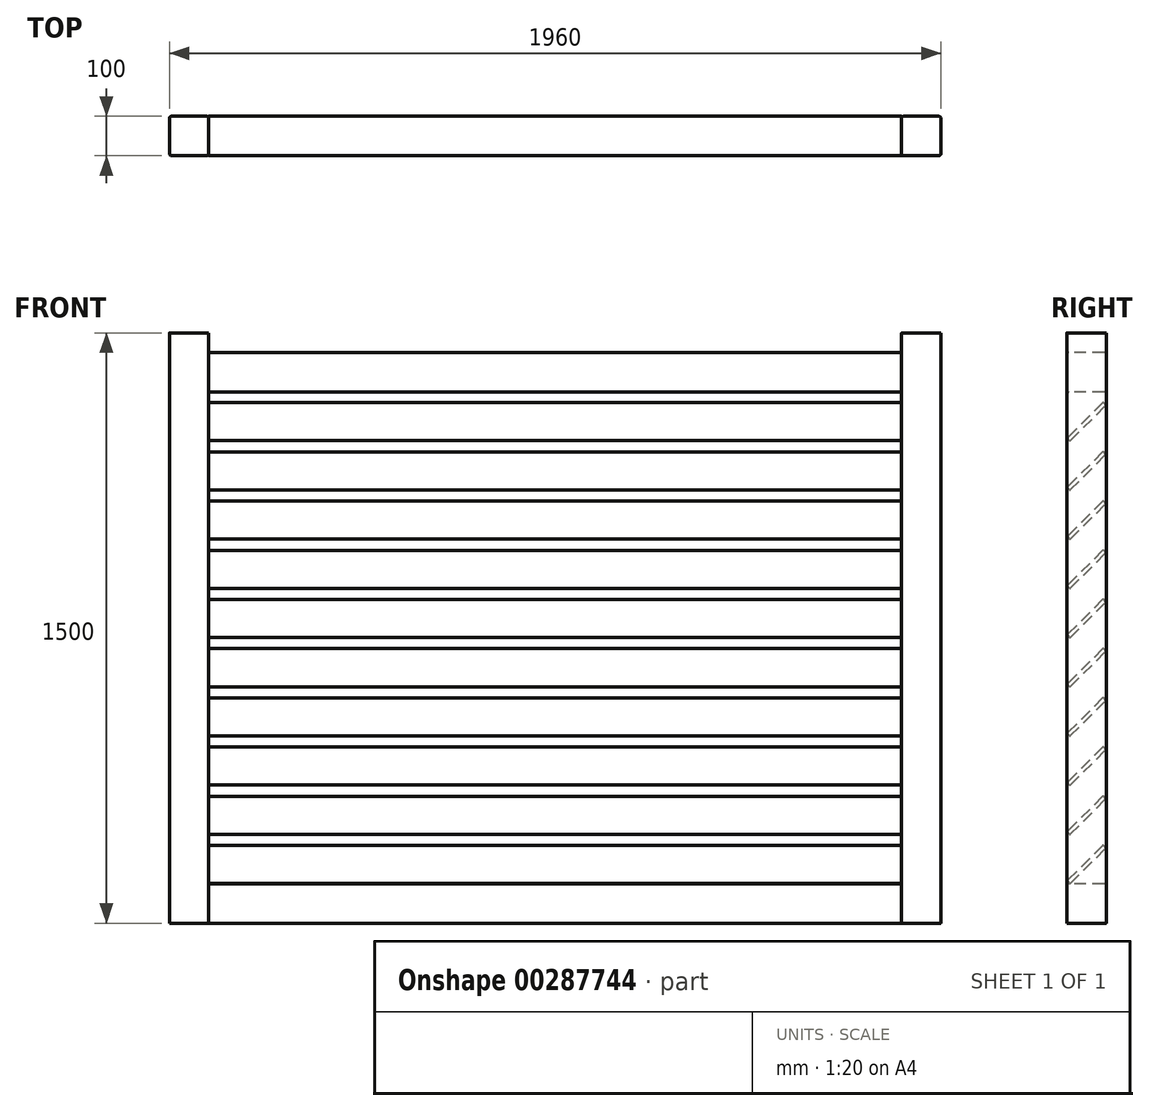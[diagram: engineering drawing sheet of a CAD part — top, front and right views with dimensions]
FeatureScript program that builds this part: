
annotation { "Feature Type Name" : "Feature", "Feature Type Description" : "" }
export const myFeature = defineFeature(function(context is Context, id is Id, definition is map)
    precondition{}
    {
        {
            var Q0;
            Q0=qCreatedBy(makeId("Right.planeOp"),FACE);
            var sketch = newSketch(context, id + "F0", { "sketchPlane" : qUnion([Q0])});
            skLineSegment(sketch, "E0", {"start": v(1.41, 1.41) * mm, "end": v(89.8, 89.8) * mm});
            skLineSegment(sketch, "E1", {"start": v(89.8, 92.63) * mm, "end": v(85.56, 96.87) * mm});
            skLineSegment(sketch, "E2", {"start": v(82.73, 96.87) * mm, "end": v(-5.66, 8.49) * mm});
            skLineSegment(sketch, "E3", {"start": v(-5.66, 5.66) * mm, "end": v(-1.41, 1.41) * mm});
            skPoint(sketch, "E4.visualSharp", {"position": v(84.15, 98.29) * mm});
            skArc(sketch, "E4.filletArc", {"start": v(85.56, 96.87) * mm, "mid": v(84.15, 97.46) * mm, "end": v(82.73, 96.87) * mm});
            skPoint(sketch, "E5.visualSharp", {"position": v(91.22, 91.22) * mm});
            skArc(sketch, "E5.filletArc", {"start": v(89.8, 89.8) * mm, "mid": v(90.39, 91.22) * mm, "end": v(89.8, 92.63) * mm});
            skPoint(sketch, "E6.visualSharp", {"position": v(0, 0) * mm});
            skArc(sketch, "E6.filletArc", {"start": v(-1.41, 1.41) * mm, "mid": v(0, 0.83) * mm, "end": v(1.41, 1.41) * mm});
            skPoint(sketch, "E7.visualSharp", {"position": v(-7.07, 7.07) * mm});
            skArc(sketch, "E7.filletArc", {"start": v(-5.66, 8.49) * mm, "mid": v(-6.24, 7.07) * mm, "end": v(-5.66, 5.66) * mm});
            skLineSegment(sketch, "E8.0.1.0", {"start": v(1.41, 126.41) * mm, "end": v(89.8, 214.8) * mm});
            skLineSegment(sketch, "E8.0.1.1", {"start": v(82.73, 221.87) * mm, "end": v(-5.66, 133.49) * mm});
            skPoint(sketch, "E8.0.1.2", {"position": v(84.15, 223.29) * mm});
            skPoint(sketch, "E8.0.1.3", {"position": v(91.22, 216.22) * mm});
            skPoint(sketch, "E8.0.1.4", {"position": v(-7.07, 132.07) * mm});
            skPoint(sketch, "E8.0.1.5", {"position": v(0, 125) * mm});
            skArc(sketch, "E8.0.1.6", {"start": v(89.8, 214.8) * mm, "mid": v(90.39, 216.22) * mm, "end": v(89.8, 217.63) * mm});
            skArc(sketch, "E8.0.1.7", {"start": v(-1.41, 126.41) * mm, "mid": v(0, 125.83) * mm, "end": v(1.41, 126.41) * mm});
            skArc(sketch, "E8.0.1.8", {"start": v(85.56, 221.87) * mm, "mid": v(84.15, 222.46) * mm, "end": v(82.73, 221.87) * mm});
            skLineSegment(sketch, "E8.0.1.9", {"start": v(-5.66, 130.66) * mm, "end": v(-1.41, 126.41) * mm});
            skArc(sketch, "E8.0.1.10", {"start": v(-5.66, 133.49) * mm, "mid": v(-6.24, 132.07) * mm, "end": v(-5.66, 130.66) * mm});
            skLineSegment(sketch, "E8.0.1.11", {"start": v(89.8, 217.63) * mm, "end": v(85.56, 221.87) * mm});
            skLineSegment(sketch, "E8.0.2.0", {"start": v(1.41, 251.41) * mm, "end": v(89.8, 339.8) * mm});
            skLineSegment(sketch, "E8.0.2.1", {"start": v(82.73, 346.87) * mm, "end": v(-5.66, 258.49) * mm});
            skPoint(sketch, "E8.0.2.2", {"position": v(84.15, 348.29) * mm});
            skPoint(sketch, "E8.0.2.3", {"position": v(91.22, 341.22) * mm});
            skPoint(sketch, "E8.0.2.4", {"position": v(-7.07, 257.07) * mm});
            skPoint(sketch, "E8.0.2.5", {"position": v(0, 250) * mm});
            skArc(sketch, "E8.0.2.6", {"start": v(89.8, 339.8) * mm, "mid": v(90.39, 341.22) * mm, "end": v(89.8, 342.63) * mm});
            skArc(sketch, "E8.0.2.7", {"start": v(-1.41, 251.41) * mm, "mid": v(0, 250.83) * mm, "end": v(1.41, 251.41) * mm});
            skArc(sketch, "E8.0.2.8", {"start": v(85.56, 346.87) * mm, "mid": v(84.15, 347.46) * mm, "end": v(82.73, 346.87) * mm});
            skLineSegment(sketch, "E8.0.2.9", {"start": v(-5.66, 255.66) * mm, "end": v(-1.41, 251.41) * mm});
            skArc(sketch, "E8.0.2.10", {"start": v(-5.66, 258.49) * mm, "mid": v(-6.24, 257.07) * mm, "end": v(-5.66, 255.66) * mm});
            skLineSegment(sketch, "E8.0.2.11", {"start": v(89.8, 342.63) * mm, "end": v(85.56, 346.87) * mm});
            skLineSegment(sketch, "E8.0.3.0", {"start": v(1.41, 376.41) * mm, "end": v(89.8, 464.8) * mm});
            skLineSegment(sketch, "E8.0.3.1", {"start": v(82.73, 471.87) * mm, "end": v(-5.66, 383.49) * mm});
            skPoint(sketch, "E8.0.3.2", {"position": v(84.15, 473.29) * mm});
            skPoint(sketch, "E8.0.3.3", {"position": v(91.22, 466.22) * mm});
            skPoint(sketch, "E8.0.3.4", {"position": v(-7.07, 382.07) * mm});
            skPoint(sketch, "E8.0.3.5", {"position": v(0, 375) * mm});
            skArc(sketch, "E8.0.3.6", {"start": v(89.8, 464.8) * mm, "mid": v(90.39, 466.22) * mm, "end": v(89.8, 467.63) * mm});
            skArc(sketch, "E8.0.3.7", {"start": v(-1.41, 376.41) * mm, "mid": v(0, 375.83) * mm, "end": v(1.41, 376.41) * mm});
            skArc(sketch, "E8.0.3.8", {"start": v(85.56, 471.87) * mm, "mid": v(84.15, 472.46) * mm, "end": v(82.73, 471.87) * mm});
            skLineSegment(sketch, "E8.0.3.9", {"start": v(-5.66, 380.66) * mm, "end": v(-1.41, 376.41) * mm});
            skArc(sketch, "E8.0.3.10", {"start": v(-5.66, 383.49) * mm, "mid": v(-6.24, 382.07) * mm, "end": v(-5.66, 380.66) * mm});
            skLineSegment(sketch, "E8.0.3.11", {"start": v(89.8, 467.63) * mm, "end": v(85.56, 471.87) * mm});
            skLineSegment(sketch, "E8.0.4.0", {"start": v(1.41, 501.41) * mm, "end": v(89.8, 589.8) * mm});
            skLineSegment(sketch, "E8.0.4.1", {"start": v(82.73, 596.87) * mm, "end": v(-5.66, 508.49) * mm});
            skPoint(sketch, "E8.0.4.2", {"position": v(84.15, 598.29) * mm});
            skPoint(sketch, "E8.0.4.3", {"position": v(91.22, 591.22) * mm});
            skPoint(sketch, "E8.0.4.4", {"position": v(-7.07, 507.07) * mm});
            skPoint(sketch, "E8.0.4.5", {"position": v(0, 500) * mm});
            skArc(sketch, "E8.0.4.6", {"start": v(89.8, 589.8) * mm, "mid": v(90.39, 591.22) * mm, "end": v(89.8, 592.63) * mm});
            skArc(sketch, "E8.0.4.7", {"start": v(-1.41, 501.41) * mm, "mid": v(0, 500.83) * mm, "end": v(1.41, 501.41) * mm});
            skArc(sketch, "E8.0.4.8", {"start": v(85.56, 596.87) * mm, "mid": v(84.15, 597.46) * mm, "end": v(82.73, 596.87) * mm});
            skLineSegment(sketch, "E8.0.4.9", {"start": v(-5.66, 505.66) * mm, "end": v(-1.41, 501.41) * mm});
            skArc(sketch, "E8.0.4.10", {"start": v(-5.66, 508.49) * mm, "mid": v(-6.24, 507.07) * mm, "end": v(-5.66, 505.66) * mm});
            skLineSegment(sketch, "E8.0.4.11", {"start": v(89.8, 592.63) * mm, "end": v(85.56, 596.87) * mm});
            skLineSegment(sketch, "E8.0.5.0", {"start": v(1.41, 626.41) * mm, "end": v(89.8, 714.8) * mm});
            skLineSegment(sketch, "E8.0.5.1", {"start": v(82.73, 721.87) * mm, "end": v(-5.66, 633.49) * mm});
            skPoint(sketch, "E8.0.5.2", {"position": v(84.15, 723.29) * mm});
            skPoint(sketch, "E8.0.5.3", {"position": v(91.22, 716.22) * mm});
            skPoint(sketch, "E8.0.5.4", {"position": v(-7.07, 632.07) * mm});
            skPoint(sketch, "E8.0.5.5", {"position": v(0, 625) * mm});
            skArc(sketch, "E8.0.5.6", {"start": v(89.8, 714.8) * mm, "mid": v(90.39, 716.22) * mm, "end": v(89.8, 717.63) * mm});
            skArc(sketch, "E8.0.5.7", {"start": v(-1.41, 626.41) * mm, "mid": v(0, 625.83) * mm, "end": v(1.41, 626.41) * mm});
            skArc(sketch, "E8.0.5.8", {"start": v(85.56, 721.87) * mm, "mid": v(84.15, 722.46) * mm, "end": v(82.73, 721.87) * mm});
            skLineSegment(sketch, "E8.0.5.9", {"start": v(-5.66, 630.66) * mm, "end": v(-1.41, 626.41) * mm});
            skArc(sketch, "E8.0.5.10", {"start": v(-5.66, 633.49) * mm, "mid": v(-6.24, 632.07) * mm, "end": v(-5.66, 630.66) * mm});
            skLineSegment(sketch, "E8.0.5.11", {"start": v(89.8, 717.63) * mm, "end": v(85.56, 721.87) * mm});
            skLineSegment(sketch, "E8.0.6.0", {"start": v(1.41, 751.41) * mm, "end": v(89.8, 839.8) * mm});
            skLineSegment(sketch, "E8.0.6.1", {"start": v(82.73, 846.87) * mm, "end": v(-5.66, 758.49) * mm});
            skPoint(sketch, "E8.0.6.2", {"position": v(84.15, 848.29) * mm});
            skPoint(sketch, "E8.0.6.3", {"position": v(91.22, 841.22) * mm});
            skPoint(sketch, "E8.0.6.4", {"position": v(-7.07, 757.07) * mm});
            skPoint(sketch, "E8.0.6.5", {"position": v(0, 750) * mm});
            skArc(sketch, "E8.0.6.6", {"start": v(89.8, 839.8) * mm, "mid": v(90.39, 841.22) * mm, "end": v(89.8, 842.63) * mm});
            skArc(sketch, "E8.0.6.7", {"start": v(-1.41, 751.41) * mm, "mid": v(0, 750.83) * mm, "end": v(1.41, 751.41) * mm});
            skArc(sketch, "E8.0.6.8", {"start": v(85.56, 846.87) * mm, "mid": v(84.15, 847.46) * mm, "end": v(82.73, 846.87) * mm});
            skLineSegment(sketch, "E8.0.6.9", {"start": v(-5.66, 755.66) * mm, "end": v(-1.41, 751.41) * mm});
            skArc(sketch, "E8.0.6.10", {"start": v(-5.66, 758.49) * mm, "mid": v(-6.24, 757.07) * mm, "end": v(-5.66, 755.66) * mm});
            skLineSegment(sketch, "E8.0.6.11", {"start": v(89.8, 842.63) * mm, "end": v(85.56, 846.87) * mm});
            skLineSegment(sketch, "E8.0.7.0", {"start": v(1.41, 876.41) * mm, "end": v(89.8, 964.8) * mm});
            skLineSegment(sketch, "E8.0.7.1", {"start": v(82.73, 971.87) * mm, "end": v(-5.66, 883.49) * mm});
            skPoint(sketch, "E8.0.7.2", {"position": v(84.15, 973.29) * mm});
            skPoint(sketch, "E8.0.7.3", {"position": v(91.22, 966.22) * mm});
            skPoint(sketch, "E8.0.7.4", {"position": v(-7.07, 882.07) * mm});
            skPoint(sketch, "E8.0.7.5", {"position": v(0, 875) * mm});
            skArc(sketch, "E8.0.7.6", {"start": v(89.8, 964.8) * mm, "mid": v(90.39, 966.22) * mm, "end": v(89.8, 967.63) * mm});
            skArc(sketch, "E8.0.7.7", {"start": v(-1.41, 876.41) * mm, "mid": v(0, 875.83) * mm, "end": v(1.41, 876.41) * mm});
            skArc(sketch, "E8.0.7.8", {"start": v(85.56, 971.87) * mm, "mid": v(84.15, 972.46) * mm, "end": v(82.73, 971.87) * mm});
            skLineSegment(sketch, "E8.0.7.9", {"start": v(-5.66, 880.66) * mm, "end": v(-1.41, 876.41) * mm});
            skArc(sketch, "E8.0.7.10", {"start": v(-5.66, 883.49) * mm, "mid": v(-6.24, 882.07) * mm, "end": v(-5.66, 880.66) * mm});
            skLineSegment(sketch, "E8.0.7.11", {"start": v(89.8, 967.63) * mm, "end": v(85.56, 971.87) * mm});
            skLineSegment(sketch, "E8.direction1", {"start": v(0, 0) * mm, "end": v(25, 0) * mm, "construction": true});
            skLineSegment(sketch, "E8.direction2", {"start": v(0, 0) * mm, "end": v(0, 125) * mm, "construction": true});
            skLineSegment(sketch, "E9.0.0.8", {"start": v(1.41, 1001.41) * mm, "end": v(89.8, 1089.8) * mm});
            skLineSegment(sketch, "E9.3.0.8", {"start": v(82.73, 1096.87) * mm, "end": v(-5.66, 1008.49) * mm});
            skPoint(sketch, "E9.6.0.8", {"position": v(84.15, 1098.29) * mm});
            skPoint(sketch, "E9.7.0.8", {"position": v(91.22, 1091.22) * mm});
            skPoint(sketch, "E9.8.0.8", {"position": v(-7.07, 1007.07) * mm});
            skPoint(sketch, "E9.9.0.8", {"position": v(0, 1000) * mm});
            skArc(sketch, "E9.10.0.8", {"start": v(89.8, 1089.8) * mm, "mid": v(90.39, 1091.22) * mm, "end": v(89.8, 1092.63) * mm});
            skArc(sketch, "E9.14.0.8", {"start": v(-1.41, 1001.41) * mm, "mid": v(0, 1000.83) * mm, "end": v(1.41, 1001.41) * mm});
            skArc(sketch, "E9.18.0.8", {"start": v(85.56, 1096.87) * mm, "mid": v(84.15, 1097.46) * mm, "end": v(82.73, 1096.87) * mm});
            skLineSegment(sketch, "E9.22.0.8", {"start": v(-5.66, 1005.66) * mm, "end": v(-1.41, 1001.41) * mm});
            skArc(sketch, "E9.25.0.8", {"start": v(-5.66, 1008.49) * mm, "mid": v(-6.24, 1007.07) * mm, "end": v(-5.66, 1005.66) * mm});
            skLineSegment(sketch, "E9.29.0.8", {"start": v(89.8, 1092.63) * mm, "end": v(85.56, 1096.87) * mm});
            skLineSegment(sketch, "E9.0.0.9", {"start": v(1.41, 1126.41) * mm, "end": v(89.8, 1214.8) * mm});
            skLineSegment(sketch, "E9.3.0.9", {"start": v(82.73, 1221.87) * mm, "end": v(-5.66, 1133.49) * mm});
            skPoint(sketch, "E9.6.0.9", {"position": v(84.15, 1223.29) * mm});
            skPoint(sketch, "E9.7.0.9", {"position": v(91.22, 1216.22) * mm});
            skPoint(sketch, "E9.8.0.9", {"position": v(-7.07, 1132.07) * mm});
            skPoint(sketch, "E9.9.0.9", {"position": v(0, 1125) * mm});
            skArc(sketch, "E9.10.0.9", {"start": v(89.8, 1214.8) * mm, "mid": v(90.39, 1216.22) * mm, "end": v(89.8, 1217.63) * mm});
            skArc(sketch, "E9.14.0.9", {"start": v(-1.41, 1126.41) * mm, "mid": v(0, 1125.83) * mm, "end": v(1.41, 1126.41) * mm});
            skArc(sketch, "E9.18.0.9", {"start": v(85.56, 1221.87) * mm, "mid": v(84.15, 1222.46) * mm, "end": v(82.73, 1221.87) * mm});
            skLineSegment(sketch, "E9.22.0.9", {"start": v(-5.66, 1130.66) * mm, "end": v(-1.41, 1126.41) * mm});
            skArc(sketch, "E9.25.0.9", {"start": v(-5.66, 1133.49) * mm, "mid": v(-6.24, 1132.07) * mm, "end": v(-5.66, 1130.66) * mm});
            skLineSegment(sketch, "E9.29.0.9", {"start": v(89.8, 1217.63) * mm, "end": v(85.56, 1221.87) * mm});
            skSolve(sketch);
        }
        {
            var Q0;
            Q0=makeQuery(id+"F0.imprint","IMPRINT",FACE,{"disambiguationData":[TD([[makeQuery(id+"F0.imprint","IMPRINT",EDGE,{"derivedFrom":sQuery(id+"F0.wireOp",EDGE,"E0")}),1.0]])]});
            var Q1;
            Q1=makeQuery(id+"F0.imprint","IMPRINT",FACE,{"disambiguationData":[TD([[makeQuery(id+"F0.imprint","IMPRINT",EDGE,{"derivedFrom":sQuery(id+"F0.wireOp",EDGE,"E8.0.1.0")}),1.0]])]});
            var Q2;
            Q2=makeQuery(id+"F0.imprint","IMPRINT",FACE,{"disambiguationData":[TD([[makeQuery(id+"F0.imprint","IMPRINT",EDGE,{"derivedFrom":sQuery(id+"F0.wireOp",EDGE,"E8.0.2.0")}),1.0]])]});
            var Q3;
            Q3=makeQuery(id+"F0.imprint","IMPRINT",FACE,{"disambiguationData":[TD([[makeQuery(id+"F0.imprint","IMPRINT",EDGE,{"derivedFrom":sQuery(id+"F0.wireOp",EDGE,"E8.0.3.0")}),1.0]])]});
            var Q4;
            Q4=makeQuery(id+"F0.imprint","IMPRINT",FACE,{"disambiguationData":[TD([[makeQuery(id+"F0.imprint","IMPRINT",EDGE,{"derivedFrom":sQuery(id+"F0.wireOp",EDGE,"E8.0.4.0")}),1.0]])]});
            var Q5;
            Q5=makeQuery(id+"F0.imprint","IMPRINT",FACE,{"disambiguationData":[TD([[makeQuery(id+"F0.imprint","IMPRINT",EDGE,{"derivedFrom":sQuery(id+"F0.wireOp",EDGE,"E8.0.5.0")}),1.0]])]});
            var Q6;
            Q6=makeQuery(id+"F0.imprint","IMPRINT",FACE,{"disambiguationData":[TD([[makeQuery(id+"F0.imprint","IMPRINT",EDGE,{"derivedFrom":sQuery(id+"F0.wireOp",EDGE,"E8.0.6.0")}),1.0]])]});
            var Q7;
            Q7=makeQuery(id+"F0.imprint","IMPRINT",FACE,{"disambiguationData":[TD([[makeQuery(id+"F0.imprint","IMPRINT",EDGE,{"derivedFrom":sQuery(id+"F0.wireOp",EDGE,"E8.0.7.0")}),1.0]])]});
            var Q8;
            Q8=makeQuery(id+"F0.imprint","IMPRINT",FACE,{"disambiguationData":[TD([[makeQuery(id+"F0.imprint","IMPRINT",EDGE,{"derivedFrom":sQuery(id+"F0.wireOp",EDGE,"E8.0.8.0")}),1.0]])]});
            var Q9;
            Q9=makeQuery(id+"F0.imprint","IMPRINT",FACE,{"disambiguationData":[TD([[makeQuery(id+"F0.imprint","IMPRINT",EDGE,{"derivedFrom":sQuery(id+"F0.wireOp",EDGE,"E8.0.9.0")}),1.0]])]});
            var Q10;
            Q10=makeQuery(id+"F0.imprint","IMPRINT",FACE,{"disambiguationData":[TD([[makeQuery(id+"F0.imprint","IMPRINT",EDGE,{"derivedFrom":sQuery(id+"F0.wireOp",EDGE,"E8.0.10.0")}),1.0]])]});
            var Q11;
            Q11=makeQuery(id+"F0.imprint","IMPRINT",FACE,{"disambiguationData":[TD([[makeQuery(id+"F0.imprint","IMPRINT",EDGE,{"derivedFrom":sQuery(id+"F0.wireOp",EDGE,"E8.0.28.0")}),1.0]])]});
            var Q12;
            Q12=makeQuery(id+"F0.imprint","IMPRINT",FACE,{"disambiguationData":[TD([[makeQuery(id+"F0.imprint","IMPRINT",EDGE,{"derivedFrom":sQuery(id+"F0.wireOp",EDGE,"E8.0.27.0")}),1.0]])]});
            var Q13;
            Q13=makeQuery(id+"F0.imprint","IMPRINT",FACE,{"disambiguationData":[TD([[makeQuery(id+"F0.imprint","IMPRINT",EDGE,{"derivedFrom":sQuery(id+"F0.wireOp",EDGE,"E8.0.26.0")}),1.0]])]});
            var Q14;
            Q14=makeQuery(id+"F0.imprint","IMPRINT",FACE,{"disambiguationData":[TD([[makeQuery(id+"F0.imprint","IMPRINT",EDGE,{"derivedFrom":sQuery(id+"F0.wireOp",EDGE,"E8.0.29.0")}),1.0]])]});
            var Q15;
            Q15=makeQuery(id+"F0.imprint","IMPRINT",FACE,{"disambiguationData":[TD([[makeQuery(id+"F0.imprint","IMPRINT",EDGE,{"derivedFrom":sQuery(id+"F0.wireOp",EDGE,"E8.0.16.0")}),1.0]])]});
            var Q16;
            Q16=makeQuery(id+"F0.imprint","IMPRINT",FACE,{"disambiguationData":[TD([[makeQuery(id+"F0.imprint","IMPRINT",EDGE,{"derivedFrom":sQuery(id+"F0.wireOp",EDGE,"E8.0.17.0")}),1.0]])]});
            var Q17;
            Q17=makeQuery(id+"F0.imprint","IMPRINT",FACE,{"disambiguationData":[TD([[makeQuery(id+"F0.imprint","IMPRINT",EDGE,{"derivedFrom":sQuery(id+"F0.wireOp",EDGE,"E8.0.18.0")}),1.0]])]});
            var Q18;
            Q18=makeQuery(id+"F0.imprint","IMPRINT",FACE,{"disambiguationData":[TD([[makeQuery(id+"F0.imprint","IMPRINT",EDGE,{"derivedFrom":sQuery(id+"F0.wireOp",EDGE,"E8.0.19.0")}),1.0]])]});
            var Q19;
            Q19=makeQuery(id+"F0.imprint","IMPRINT",FACE,{"disambiguationData":[TD([[makeQuery(id+"F0.imprint","IMPRINT",EDGE,{"derivedFrom":sQuery(id+"F0.wireOp",EDGE,"E8.0.20.0")}),1.0]])]});
            var Q20;
            Q20=makeQuery(id+"F0.imprint","IMPRINT",FACE,{"disambiguationData":[TD([[makeQuery(id+"F0.imprint","IMPRINT",EDGE,{"derivedFrom":sQuery(id+"F0.wireOp",EDGE,"E8.0.21.0")}),1.0]])]});
            var Q21;
            Q21=makeQuery(id+"F0.imprint","IMPRINT",FACE,{"disambiguationData":[TD([[makeQuery(id+"F0.imprint","IMPRINT",EDGE,{"derivedFrom":sQuery(id+"F0.wireOp",EDGE,"E8.0.22.0")}),1.0]])]});
            var Q22;
            Q22=makeQuery(id+"F0.imprint","IMPRINT",FACE,{"disambiguationData":[TD([[makeQuery(id+"F0.imprint","IMPRINT",EDGE,{"derivedFrom":sQuery(id+"F0.wireOp",EDGE,"E8.0.15.0")}),1.0]])]});
            var Q23;
            Q23=makeQuery(id+"F0.imprint","IMPRINT",FACE,{"disambiguationData":[TD([[makeQuery(id+"F0.imprint","IMPRINT",EDGE,{"derivedFrom":sQuery(id+"F0.wireOp",EDGE,"E8.0.13.0")}),1.0]])]});
            var Q24;
            Q24=makeQuery(id+"F0.imprint","IMPRINT",FACE,{"disambiguationData":[TD([[makeQuery(id+"F0.imprint","IMPRINT",EDGE,{"derivedFrom":sQuery(id+"F0.wireOp",EDGE,"E8.0.14.0")}),1.0]])]});
            var Q25;
            Q25=makeQuery(id+"F0.imprint","IMPRINT",FACE,{"disambiguationData":[TD([[makeQuery(id+"F0.imprint","IMPRINT",EDGE,{"derivedFrom":sQuery(id+"F0.wireOp",EDGE,"E8.0.11.0")}),1.0]])]});
            var Q26;
            Q26=makeQuery(id+"F0.imprint","IMPRINT",FACE,{"disambiguationData":[TD([[makeQuery(id+"F0.imprint","IMPRINT",EDGE,{"derivedFrom":sQuery(id+"F0.wireOp",EDGE,"E8.0.12.0")}),1.0]])]});
            var Q27;
            Q27=makeQuery(id+"F0.imprint","IMPRINT",FACE,{"disambiguationData":[TD([[makeQuery(id+"F0.imprint","IMPRINT",EDGE,{"derivedFrom":sQuery(id+"F0.wireOp",EDGE,"E8.0.23.0")}),1.0]])]});
            var Q28;
            Q28=makeQuery(id+"F0.imprint","IMPRINT",FACE,{"disambiguationData":[TD([[makeQuery(id+"F0.imprint","IMPRINT",EDGE,{"derivedFrom":sQuery(id+"F0.wireOp",EDGE,"E8.0.24.0")}),1.0]])]});
            var Q29;
            Q29=makeQuery(id+"F0.imprint","IMPRINT",FACE,{"disambiguationData":[TD([[makeQuery(id+"F0.imprint","IMPRINT",EDGE,{"derivedFrom":sQuery(id+"F0.wireOp",EDGE,"E8.0.25.0")}),1.0]])]});
            var Q30;
            Q30=makeQuery(id+"F0.imprint","IMPRINT",FACE,{"disambiguationData":[TD([[makeQuery(id+"F0.imprint","IMPRINT",EDGE,{"derivedFrom":sQuery(id+"F0.wireOp",EDGE,"E9.0.0.8")}),1.0]])]});
            var Q31;
            Q31=makeQuery(id+"F0.imprint","IMPRINT",FACE,{"disambiguationData":[TD([[makeQuery(id+"F0.imprint","IMPRINT",EDGE,{"derivedFrom":sQuery(id+"F0.wireOp",EDGE,"E9.0.0.9")}),1.0]])]});
            var Q32;
            Q32=makeQuery(id+"F0.imprint","IMPRINT",FACE,{"disambiguationData":[TD([[makeQuery(id+"F0.imprint","IMPRINT",EDGE,{"derivedFrom":sQuery(id+"F0.wireOp",EDGE,"E9.0.0.10")}),1.0]])]});
            var Q33;
            Q33=makeQuery(id+"F0.imprint","IMPRINT",FACE,{"disambiguationData":[TD([[makeQuery(id+"F0.imprint","IMPRINT",EDGE,{"derivedFrom":sQuery(id+"F0.wireOp",EDGE,"E9.0.0.11")}),1.0]])]});
            extrude(context, id + "F1", {"entities" : qUnion([Q0, Q1, Q2, Q3, Q4, Q5, Q6, Q7, Q8, Q9, Q10, Q11, Q12, Q13, Q14, Q15, Q16, Q17, Q18, Q19, Q20, Q21, Q22, Q23, Q24, Q25, Q26, Q27, Q28, Q29, Q30, Q31, Q32, Q33]), "depth" : 1760 * mm});
        }
        {
            var Q0;
            Q0=qCreatedBy(makeId("Top.planeOp"),FACE);
            var sketch = newSketch(context, id + "F2", { "sketchPlane" : qUnion([Q0])});
            skLineSegment(sketch, "E10.bottom", {"start": v(-5, -8) * mm, "end": v(-95, -8) * mm});
            skLineSegment(sketch, "E10.top", {"start": v(-5, 92) * mm, "end": v(-95, 92) * mm});
            skLineSegment(sketch, "E10.left", {"start": v(0, -3) * mm, "end": v(0, 87) * mm});
            skLineSegment(sketch, "E10.right", {"start": v(-100, -3) * mm, "end": v(-100, 87) * mm});
            skPoint(sketch, "E11.visualSharp", {"position": v(-100, 92) * mm});
            skArc(sketch, "E11.filletArc", {"start": v(-95, 92) * mm, "mid": v(-98.54, 90.54) * mm, "end": v(-100, 87) * mm});
            skPoint(sketch, "E12.visualSharp", {"position": v(0, 92) * mm});
            skArc(sketch, "E12.filletArc", {"start": v(0, 87) * mm, "mid": v(-1.46, 90.54) * mm, "end": v(-5, 92) * mm});
            skPoint(sketch, "E13.visualSharp", {"position": v(0, -8) * mm});
            skArc(sketch, "E13.filletArc", {"start": v(-5, -8) * mm, "mid": v(-1.46, -6.54) * mm, "end": v(0, -3) * mm});
            skPoint(sketch, "E14.visualSharp", {"position": v(-100, -8) * mm});
            skArc(sketch, "E14.filletArc", {"start": v(-100, -3) * mm, "mid": v(-98.54, -6.54) * mm, "end": v(-95, -8) * mm});
            skLineSegment(sketch, "E15.1.0.0", {"start": v(1760, -3) * mm, "end": v(1760, 87) * mm});
            skLineSegment(sketch, "E15.1.0.1", {"start": v(1860, -3) * mm, "end": v(1860, 87) * mm});
            skLineSegment(sketch, "E15.1.0.2", {"start": v(1855, -8) * mm, "end": v(1765, -8) * mm});
            skLineSegment(sketch, "E15.1.0.3", {"start": v(1855, 92) * mm, "end": v(1765, 92) * mm});
            skPoint(sketch, "E15.1.0.4", {"position": v(1760, 92) * mm});
            skPoint(sketch, "E15.1.0.5", {"position": v(1760, -8) * mm});
            skPoint(sketch, "E15.1.0.6", {"position": v(1860, 92) * mm});
            skPoint(sketch, "E15.1.0.7", {"position": v(1860, -8) * mm});
            skArc(sketch, "E15.1.0.8", {"start": v(1760, -3) * mm, "mid": v(1761.46, -6.54) * mm, "end": v(1765, -8) * mm});
            skArc(sketch, "E15.1.0.9", {"start": v(1860, 87) * mm, "mid": v(1858.54, 90.54) * mm, "end": v(1855, 92) * mm});
            skArc(sketch, "E15.1.0.10", {"start": v(1855, -8) * mm, "mid": v(1858.54, -6.54) * mm, "end": v(1860, -3) * mm});
            skArc(sketch, "E15.1.0.11", {"start": v(1765, 92) * mm, "mid": v(1761.46, 90.54) * mm, "end": v(1760, 87) * mm});
            skLineSegment(sketch, "E15.direction1", {"start": v(-100, -8) * mm, "end": v(1760, -8) * mm, "construction": true});
            skSolve(sketch);
        }
        {
            var Q0;
            Q0=makeQuery(id+"F2.imprint","IMPRINT",FACE,{"disambiguationData":[TD([[makeQuery(id+"F2.imprint","IMPRINT",EDGE,{"derivedFrom":sQuery(id+"F2.wireOp",EDGE,"E10.bottom")}),-1.0]])]});
            var Q1;
            Q1=makeQuery(id+"F2.imprint","IMPRINT",FACE,{"disambiguationData":[TD([[makeQuery(id+"F2.imprint","IMPRINT",EDGE,{"derivedFrom":sQuery(id+"F2.wireOp",EDGE,"E15.1.0.0")}),-1.0]])]});
            extrude(context, id + "F3", {"entities" : qUnion([Q0, Q1]), "depth" : 1400 * mm, "hasSecondDirection" : true, "secondDirectionOppositeDirection" : true, "secondDirectionDepth" : 100 * mm});
        }
        {
            var Q0;
            Q0=makeQuery(id+"F3.opExtrude","SWEPT_FACE",FACE,{"disambiguationData":[OSD([sQuery(id+"F2.wireOp",EDGE,"E10.left")])]});
            var sketch = newSketch(context, id + "F4", { "sketchPlane" : qUnion([Q0])});
            skLineSegment(sketch, "E16.bottom", {"start": v(87, -100) * mm, "end": v(-3, -100) * mm});
            skLineSegment(sketch, "E16.top", {"start": v(87, 0) * mm, "end": v(-3, 0) * mm});
            skLineSegment(sketch, "E16.left", {"start": v(92, -95) * mm, "end": v(92, -5) * mm});
            skLineSegment(sketch, "E16.right", {"start": v(-8, -95) * mm, "end": v(-8, -5) * mm});
            skPoint(sketch, "E17.visualSharp", {"position": v(92, 0) * mm});
            skArc(sketch, "E17.filletArc", {"start": v(92, -5) * mm, "mid": v(90.54, -1.46) * mm, "end": v(87, 0) * mm});
            skPoint(sketch, "E18.visualSharp", {"position": v(92, -100) * mm});
            skArc(sketch, "E18.filletArc", {"start": v(87, -100) * mm, "mid": v(90.54, -98.54) * mm, "end": v(92, -95) * mm});
            skPoint(sketch, "E19.visualSharp", {"position": v(-8, -100) * mm});
            skArc(sketch, "E19.filletArc", {"start": v(-8, -95) * mm, "mid": v(-6.54, -98.54) * mm, "end": v(-3, -100) * mm});
            skPoint(sketch, "E20.visualSharp", {"position": v(-8, 0) * mm});
            skArc(sketch, "E20.filletArc", {"start": v(-3, 0) * mm, "mid": v(-6.54, -1.46) * mm, "end": v(-8, -5) * mm});
            skLineSegment(sketch, "E21.0.1.0", {"start": v(87, 1250) * mm, "end": v(-3, 1250) * mm});
            skPoint(sketch, "E21.0.1.1", {"position": v(-8, 1250) * mm});
            skPoint(sketch, "E21.0.1.2", {"position": v(-8, 1350) * mm});
            skLineSegment(sketch, "E21.0.1.3", {"start": v(-8, 1255) * mm, "end": v(-8, 1345) * mm});
            skPoint(sketch, "E21.0.1.4", {"position": v(92, 1350) * mm});
            skPoint(sketch, "E21.0.1.5", {"position": v(92, 1250) * mm});
            skLineSegment(sketch, "E21.0.1.6", {"start": v(92, 1255) * mm, "end": v(92, 1345) * mm});
            skLineSegment(sketch, "E21.0.1.7", {"start": v(87, 1350) * mm, "end": v(-3, 1350) * mm});
            skArc(sketch, "E21.0.1.8", {"start": v(-3, 1350) * mm, "mid": v(-6.54, 1348.54) * mm, "end": v(-8, 1345) * mm});
            skArc(sketch, "E21.0.1.9", {"start": v(-8, 1255) * mm, "mid": v(-6.54, 1251.46) * mm, "end": v(-3, 1250) * mm});
            skArc(sketch, "E21.0.1.10", {"start": v(87, 1250) * mm, "mid": v(90.54, 1251.46) * mm, "end": v(92, 1255) * mm});
            skArc(sketch, "E21.0.1.11", {"start": v(92, 1345) * mm, "mid": v(90.54, 1348.54) * mm, "end": v(87, 1350) * mm});
            skLineSegment(sketch, "E21.direction1", {"start": v(-8, -100) * mm, "end": v(17, -100) * mm, "construction": true});
            skLineSegment(sketch, "E21.direction2", {"start": v(-8, -100) * mm, "end": v(-8, 1250) * mm, "construction": true});
            skSolve(sketch);
        }
        {
            var Q0;
            {var subQ0=sQuery(id+"F4.wireOp",EDGE,"E21.0.1.0");Q0=makeQuery(id+"F4.imprint","IMPRINT",FACE,{"disambiguationData":[TD([[makeQuery(id+"F4.imprint","IMPRINT",EDGE,{"derivedFrom":subQ0}),-1.0]])]});}
            var Q1;
            {var subQ0=sQuery(id+"F4.wireOp",EDGE,"E16.bottom");Q1=makeQuery(id+"F4.imprint","IMPRINT",FACE,{"disambiguationData":[TD([[makeQuery(id+"F4.imprint","IMPRINT",EDGE,{"derivedFrom":subQ0}),1.0]])]});}
            var Q2;
            Q2=makeQuery(id+"F4.imprint","IMPRINT",FACE,{"disambiguationData":[TD([[makeQuery(id+"F4.imprint","IMPRINT",EDGE,{"derivedFrom":sQuery(id+"F4.wireOp",EDGE,"E21.0.1.3")}),-1.0]])]});
            var Q3;
            Q3=makeQuery(id+"F4.imprint","IMPRINT",FACE,{"disambiguationData":[TD([[makeQuery(id+"F4.imprint","IMPRINT",EDGE,{"derivedFrom":sQuery(id+"F4.wireOp",EDGE,"E16.right")}),-1.0]])]});
            var Q4;
            Q4=makeQuery(id+"F4.imprint","IMPRINT",FACE,{"disambiguationData":[TD([[makeQuery(id+"F4.imprint","IMPRINT",EDGE,{"derivedFrom":sQuery(id+"F4.wireOp",EDGE,"E21.0.1.6")}),1.0]])]});
            var Q5;
            Q5=makeQuery(id+"F4.imprint","IMPRINT",FACE,{"disambiguationData":[TD([[makeQuery(id+"F4.imprint","IMPRINT",EDGE,{"derivedFrom":sQuery(id+"F4.wireOp",EDGE,"E16.left")}),1.0]])]});
            extrude(context, id + "F5", {"entities" : qUnion([Q0, Q1, Q2, Q3, Q4, Q5]), "depth" : 1760 * mm});
        }
    });
